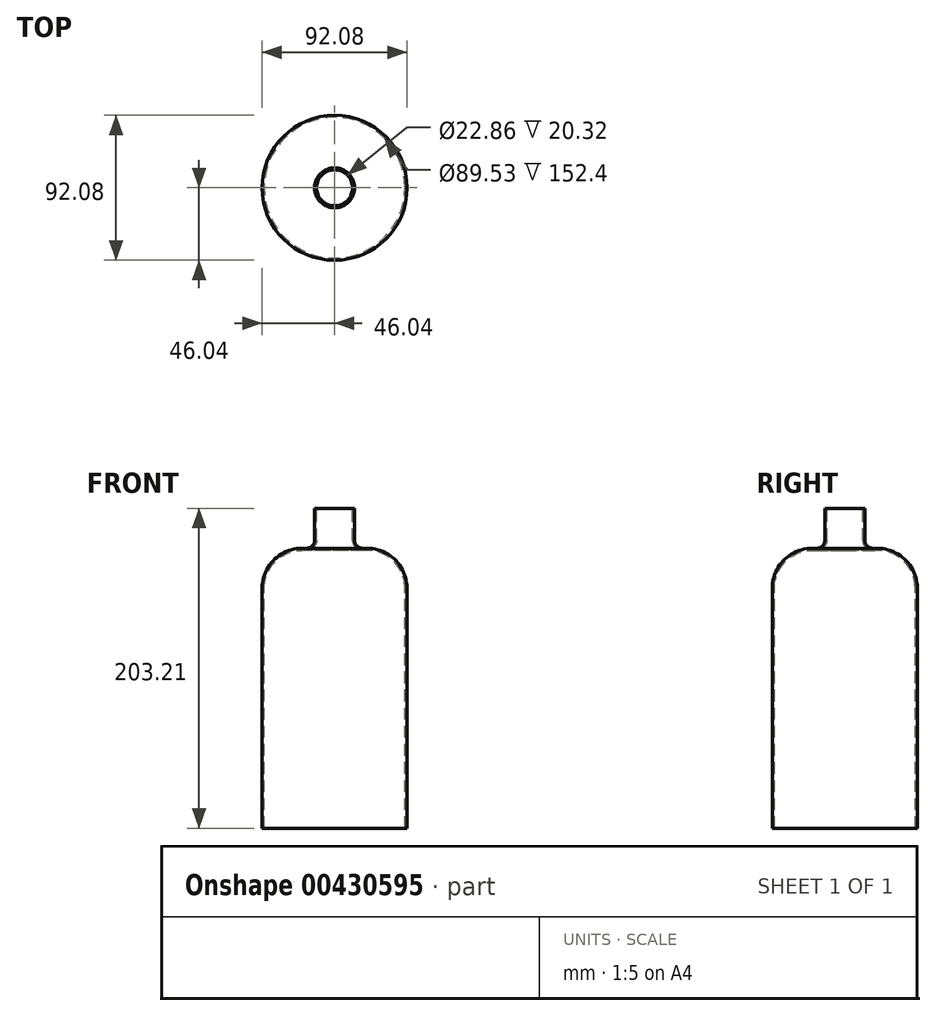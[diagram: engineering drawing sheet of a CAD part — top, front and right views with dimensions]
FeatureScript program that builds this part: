
annotation { "Feature Type Name" : "Feature", "Feature Type Description" : "" }
export const myFeature = defineFeature(function(context is Context, id is Id, definition is map)
    precondition{}
    {
        {
            var Q0;
            Q0=qCreatedBy(makeId("Front.planeOp"),FACE);
            var sketch = newSketch(context, id + "F0", { "sketchPlane" : qUnion([Q0])});
            skLineSegment(sketch, "E0.top", {"start": v(-11.43, 104.78) * mm, "end": v(-12.7, 104.78) * mm});
            skLineSegment(sketch, "E0.right", {"start": v(-46.04, -98.42) * mm, "end": v(-46.04, 53.97) * mm});
            skPoint(sketch, "E0.middle", {"position": v(0, 0) * mm});
            skLineSegment(sketch, "E1", {"start": v(0, 104.78) * mm, "end": v(0, -104.78) * mm});
            skLineSegment(sketch, "E2", {"start": v(-17.78, 79.37) * mm, "end": v(-20.64, 79.37) * mm});
            skArc(sketch, "E3.filletArc", {"start": v(-20.64, 79.38) * mm, "mid": v(-38.6, 71.94) * mm, "end": v(-46.04, 53.97) * mm});
            skPoint(sketch, "E4.visualSharp", {"position": v(-12.7, 79.38) * mm});
            skLineSegment(sketch, "E5", {"start": v(-12.7, 84.45) * mm, "end": v(-12.7, 104.78) * mm});
            skPoint(sketch, "E6.visualSharp", {"position": v(-12.7, 79.37) * mm});
            skArc(sketch, "E6.filletArc", {"start": v(-17.78, 79.38) * mm, "mid": v(-14.19, 80.86) * mm, "end": v(-12.7, 84.45) * mm});
            skLineSegment(sketch, "E7.0", {"start": v(-11.43, 84.45) * mm, "end": v(-11.43, 104.78) * mm});
            skArc(sketch, "E7.1", {"start": v(-17.78, 78.1) * mm, "mid": v(-13.29, 79.96) * mm, "end": v(-11.43, 84.45) * mm});
            skLineSegment(sketch, "E7.3", {"start": v(-44.77, -98.42) * mm, "end": v(-44.77, 53.97) * mm});
            skArc(sketch, "E7.4", {"start": v(-20.64, 78.1) * mm, "mid": v(-37.7, 71.04) * mm, "end": v(-44.77, 53.97) * mm});
            skLineSegment(sketch, "E7.5", {"start": v(-17.78, 78.1) * mm, "end": v(-20.64, 78.1) * mm});
            skLineSegment(sketch, "E8", {"start": v(-46.04, -98.42) * mm, "end": v(-44.77, -98.42) * mm});
            skSolve(sketch);
        }
        {
            var Q0;
            Q0=qSketchRegion(id+"F0",true);
            var Q1;
            Q1=sQuery(id+"F0.wireOp",EDGE,"E1");
            revolve(context, id + "F1", {"entities" : qUnion([Q0]), "axis" : qUnion([Q1]), "revolveType" : RevolveType.FULL});
        }
    });
